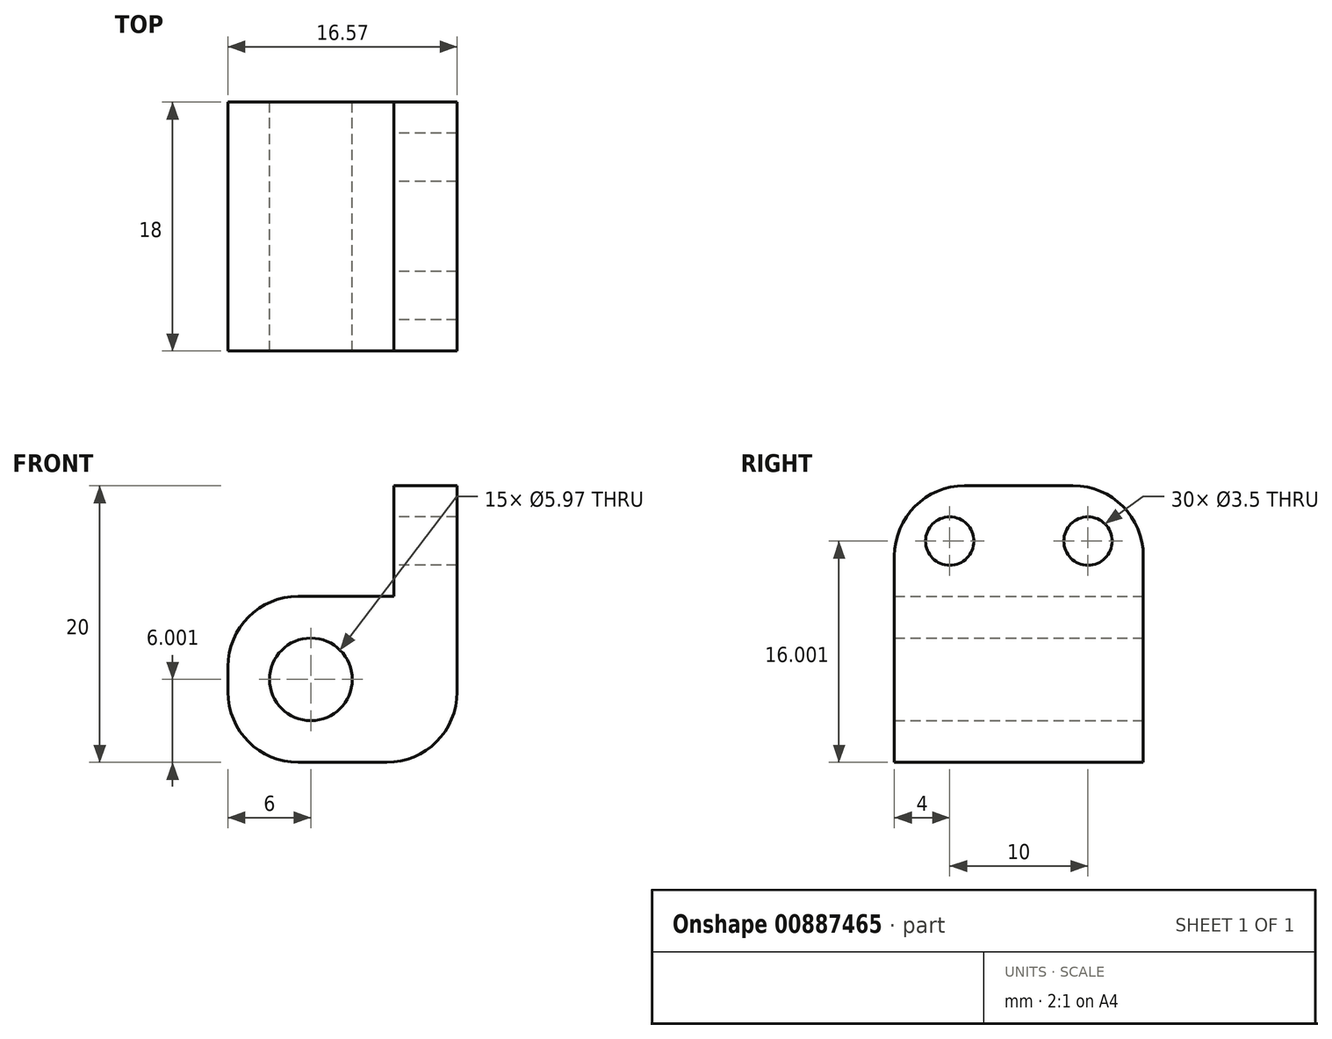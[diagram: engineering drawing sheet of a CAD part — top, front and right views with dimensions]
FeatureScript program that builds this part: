
annotation { "Feature Type Name" : "Feature", "Feature Type Description" : "" }
export const myFeature = defineFeature(function(context is Context, id is Id, definition is map)
    precondition{}
    {
        {
            var Q0;
            Q0=qCreatedBy(makeId("Front.planeOp"),FACE);
            var sketch = newSketch(context, id + "F0", { "sketchPlane" : qUnion([Q0])});
            skLineSegment(sketch, "E0.bottom", {"start": v(-20.07, 34.9) * mm, "end": v(-8.07, 34.9) * mm});
            skLineSegment(sketch, "E0.top", {"start": v(-20.07, 22.9) * mm, "end": v(-8.07, 22.9) * mm});
            skLineSegment(sketch, "E0.left", {"start": v(-20.07, 34.9) * mm, "end": v(-20.07, 22.9) * mm});
            skLineSegment(sketch, "E0.right", {"start": v(-8.07, 34.9) * mm, "end": v(-8.07, 22.9) * mm});
            skLineSegment(sketch, "E1.bottom", {"start": v(-8.07, 22.9) * mm, "end": v(-3.5, 22.9) * mm});
            skLineSegment(sketch, "E1.top", {"start": v(-8.07, 42.9) * mm, "end": v(-3.5, 42.9) * mm});
            skLineSegment(sketch, "E1.left", {"start": v(-8.07, 22.9) * mm, "end": v(-8.07, 42.9) * mm});
            skLineSegment(sketch, "E1.right", {"start": v(-3.5, 22.9) * mm, "end": v(-3.5, 42.9) * mm});
            skCircle(sketch, "E2", {"center": v(-14.07, 28.9) * mm, "radius": 2.98 * mm});
            skSolve(sketch);
        }
        {
            var Q0;
            {var subQ2=sQuery(id+"F0.wireOp",EDGE,"E0.bottom");Q0=makeQuery(id+"F0.imprint","IMPRINT",FACE,{"disambiguationData":[TD([[makeQuery(id+"F0.imprint","IMPRINT",EDGE,{"derivedFrom":subQ2}),-1.0]])]});}
            var Q1;
            {var subQ3=sQuery(id+"F0.wireOp",EDGE,"E1.bottom");Q1=makeQuery(id+"F0.imprint","IMPRINT",FACE,{"disambiguationData":[TD([[makeQuery(id+"F0.imprint","IMPRINT",EDGE,{"derivedFrom":subQ3}),1.0]])]});}
            extrude(context, id + "F1", {"entities" : qUnion([Q0, Q1]), "depth" : 18 * mm, "offsetDistance" : 25.4 * mm});
        }
        {
            var Q0;
            Q0=makeQuery(id+"F1.opExtrude","SWEPT_FACE",FACE,{"disambiguationData":[OSD([sQuery(id+"F0.wireOp",EDGE,"E1.left")])]});
            var sketch = newSketch(context, id + "F2", { "sketchPlane" : qUnion([Q0])});
            skCircle(sketch, "E3", {"center": v(4, 38.9) * mm, "radius": 1.75 * mm});
            skCircle(sketch, "E4", {"center": v(14, 38.9) * mm, "radius": 1.75 * mm});
            skSolve(sketch);
        }
        {
            var Q0;
            Q0=makeQuery(id+"F2.imprint","IMPRINT",FACE,{"disambiguationData":[TD([[makeQuery(id+"F2.imprint","IMPRINT",EDGE,{"derivedFrom":sQuery(id+"F2.wireOp",EDGE,"E3")}),1.0]])]});
            var Q1;
            Q1=makeQuery(id+"F2.imprint","IMPRINT",FACE,{"disambiguationData":[TD([[makeQuery(id+"F2.imprint","IMPRINT",EDGE,{"derivedFrom":sQuery(id+"F2.wireOp",EDGE,"E4")}),1.0]])]});
            extrude(context, id + "F3", {"entities" : qUnion([Q0, Q1]), "operationType" : NewBodyOperationType.REMOVE, "oppositeDirection" : true, "depth" : 25.4 * mm, "offsetDistance" : 25.4 * mm});
        }
        {
            var Q0;
            Q0=makeQuery(id+"F1.opExtrude","CAP_EDGE",EDGE,{"disambiguationData":[OSD([sQuery(id+"F0.wireOp",EDGE,"E1.top")])],"isStart":true});
            var Q1;
            Q1=makeQuery(id+"F1.opExtrude","CAP_EDGE",EDGE,{"disambiguationData":[OSD([sQuery(id+"F0.wireOp",EDGE,"E1.top")])],"isStart":false});
            var Q2;
            Q2=makeQuery(id+"F1.opExtrude","SWEPT_EDGE",EDGE,{"disambiguationData":[OSD([sQuery(id+"F0.wireOp",EDGE,"E0.bottom"),sQuery(id+"F0.wireOp",EDGE,"E0.left")])]});
            var Q3;
            Q3=makeQuery(id+"F1.opExtrude","SWEPT_EDGE",EDGE,{"disambiguationData":[OSD([sQuery(id+"F0.wireOp",EDGE,"E0.top"),sQuery(id+"F0.wireOp",EDGE,"E0.left")])]});
            var Q4;
            Q4=makeQuery(id+"F1.opExtrude","SWEPT_EDGE",EDGE,{"disambiguationData":[OSD([sQuery(id+"F0.wireOp",EDGE,"E1.bottom"),sQuery(id+"F0.wireOp",EDGE,"E1.right")])]});
            fillet(context, id + "F4", {"entities" : qUnion([Q0, Q1, Q2, Q3, Q4]), "radius" : 5.08 * mm, "tangentPropagation" : true, "allowEdgeOverflow" : false});
        }
    });
